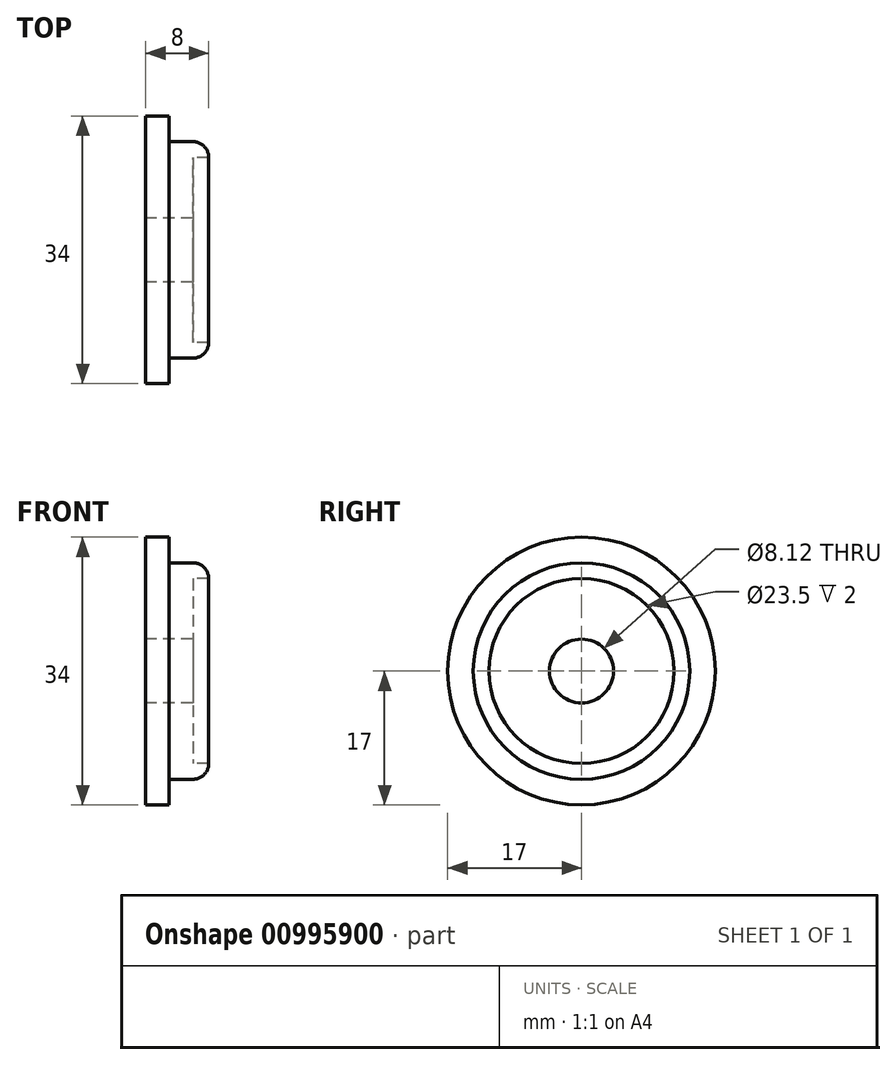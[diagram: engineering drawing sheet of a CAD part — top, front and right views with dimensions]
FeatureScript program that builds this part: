
annotation { "Feature Type Name" : "Feature", "Feature Type Description" : "" }
export const myFeature = defineFeature(function(context is Context, id is Id, definition is map)
    precondition{}
    {
        {
            var Q0;
            Q0=qCreatedBy(makeId("Front.planeOp"),FACE);
            var sketch = newSketch(context, id + "F0", { "sketchPlane" : qUnion([Q0])});
            skLineSegment(sketch, "E0", {"start": v(0, 4.06) * mm, "end": v(0, 17) * mm});
            skLineSegment(sketch, "E1", {"start": v(0, 17) * mm, "end": v(3, 17) * mm});
            skLineSegment(sketch, "E2", {"start": v(3, 17) * mm, "end": v(3, 13.75) * mm});
            skLineSegment(sketch, "E3", {"start": v(3, 13.75) * mm, "end": v(8, 13.75) * mm});
            skLineSegment(sketch, "E4", {"start": v(8, 13.75) * mm, "end": v(8, 11.75) * mm});
            skLineSegment(sketch, "E5", {"start": v(8, 11.75) * mm, "end": v(6, 11.75) * mm});
            skLineSegment(sketch, "E6", {"start": v(6, 11.75) * mm, "end": v(6, 4.06) * mm});
            skPoint(sketch, "E7.end.orphan", {"position": v(3, 0) * mm});
            skLineSegment(sketch, "E8", {"start": v(0, 4.06) * mm, "end": v(6, 4.06) * mm});
            skPoint(sketch, "E9.orphan", {"position": v(6, 0) * mm});
            skLineSegment(sketch, "E10", {"start": v(0, 0) * mm, "end": v(6.42, 0) * mm, "construction": true});
            skSolve(sketch);
        }
        {
            var Q0;
            Q0=makeQuery(id+"F0.imprint","IMPRINT",FACE,{"disambiguationData":[TD([[makeQuery(id+"F0.imprint","IMPRINT",EDGE,{"derivedFrom":sQuery(id+"F0.wireOp",EDGE,"E0")}),-1.0]])]});
            var Q1;
            Q1=sQuery(id+"F0.wireOp",EDGE,"E10");
            revolve(context, id + "F1", {"surfaceOperationType" : NewSurfaceOperationType.NEW, "entities" : qUnion([Q0]), "axis" : qUnion([Q1]), "revolveType" : RevolveType.FULL});
        }
        {
            var Q0;
            Q0=makeQuery(id+"F1.opRevolve","SWEPT_EDGE",EDGE,{"disambiguationData":[OSD([sQuery(id+"F0.wireOp",EDGE,"E3"),sQuery(id+"F0.wireOp",EDGE,"E4")])]});
            fillet(context, id + "F2", {"entities" : qUnion([Q0]), "radius" : 2 * mm, "tangentPropagation" : true, "allowEdgeOverflow" : false});
        }
    });
